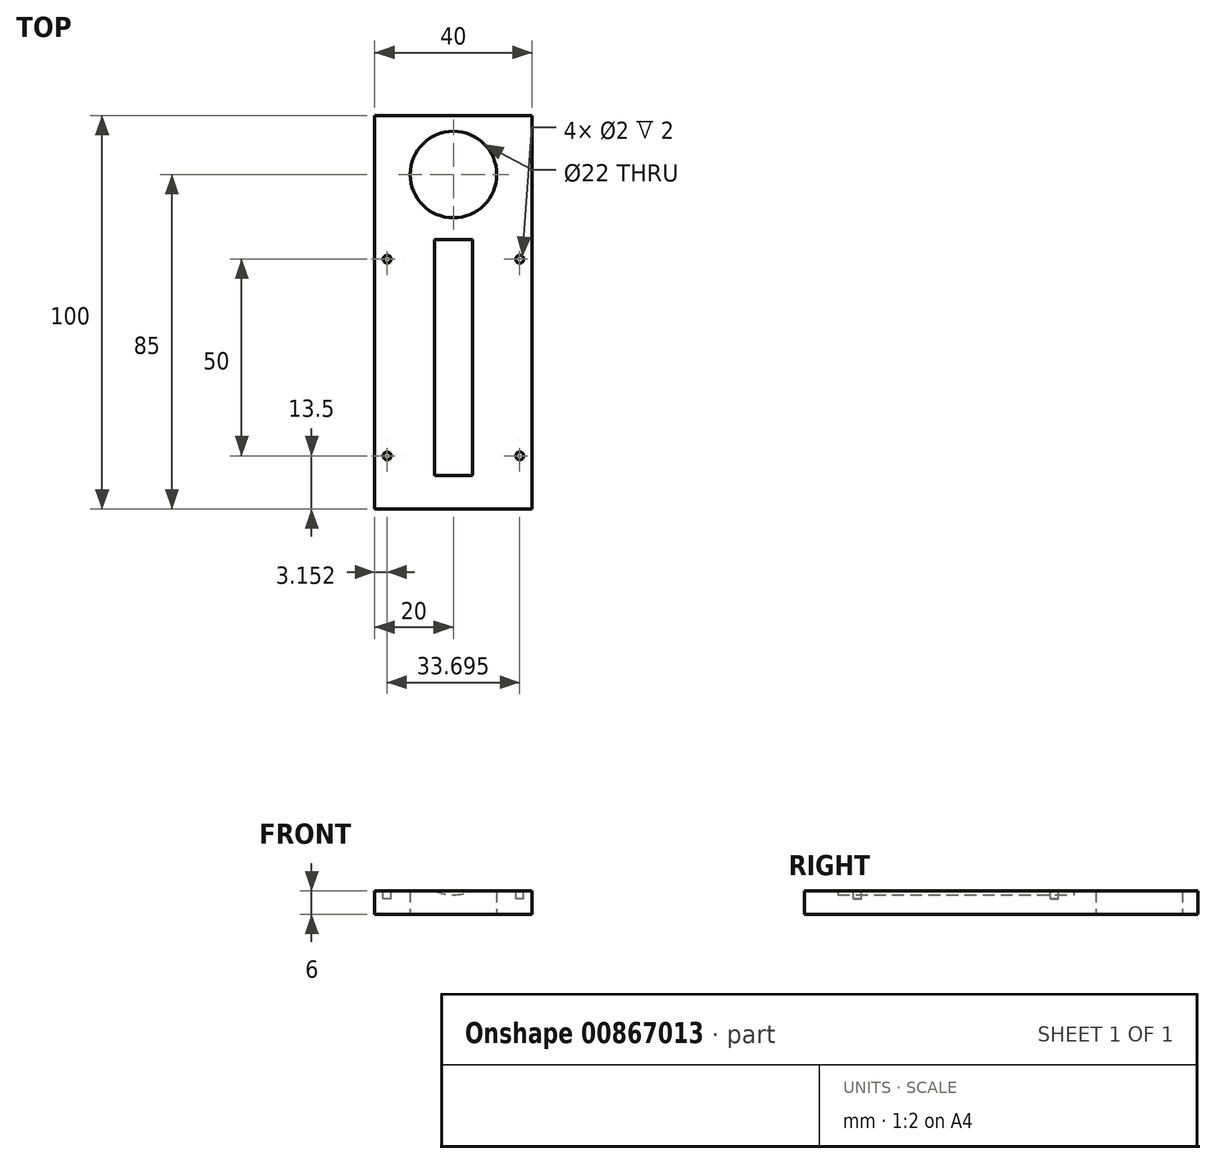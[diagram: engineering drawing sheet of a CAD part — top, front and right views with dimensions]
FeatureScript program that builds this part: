
annotation { "Feature Type Name" : "Feature", "Feature Type Description" : "" }
export const myFeature = defineFeature(function(context is Context, id is Id, definition is map)
    precondition{}
    {
        {
            var Q0;
            Q0=qCreatedBy(makeId("Top.planeOp"),FACE);
            var sketch = newSketch(context, id + "F0", { "sketchPlane" : qUnion([Q0])});
            skLineSegment(sketch, "E0.bottom", {"start": v(20, 15) * mm, "end": v(-20, 15) * mm});
            skLineSegment(sketch, "E0.top", {"start": v(20, -85) * mm, "end": v(-20, -85) * mm});
            skLineSegment(sketch, "E0.left", {"start": v(20, 15) * mm, "end": v(20, -85) * mm});
            skLineSegment(sketch, "E0.right", {"start": v(-20, 15) * mm, "end": v(-20, -85) * mm});
            skPoint(sketch, "E0.middle", {"position": v(0, 0) * mm});
            skCircle(sketch, "E1", {"center": v(0, 0) * mm, "radius": 11 * mm});
            skLineSegment(sketch, "E2", {"start": v(0, 15) * mm, "end": v(0, -33.63) * mm, "construction": true});
            skSolve(sketch);
        }
        {
            var Q0;
            Q0 = qSketchRegion(id + "F0", true);
            extrude(context, id + "F1", {"entities" : qUnion([Q0]), "depth" : 6 * mm, "offsetDistance" : 25 * mm});
        }
        {
            var Q0;
            Q0=qCreatedBy(makeId("Front.planeOp"),FACE);
            var sketch = newSketch(context, id + "F2", { "sketchPlane" : qUnion([Q0])});
            skCircle(sketch, "E3", {"center": v(0, 17.25) * mm, "radius": 12.25 * mm});
            skSolve(sketch);
        }
        {
            var Q0;
            Q0 = qSketchRegion(id + "F2", true);
            extrude(context, id + "F3", {"entities" : qUnion([Q0]), "operationType" : NewBodyOperationType.REMOVE, "depth" : (16.5 + 60) * mm, "offsetDistance" : 25 * mm, "hasSecondDirection" : true, "secondDirectionOppositeDirection" : false, "secondDirectionDepth" : 16.5 * mm});
        }
        {
            var Q0;
            Q0=makeQuery(id+"F1.opExtrude","CAP_FACE",FACE,{"disambiguationData":[OSD([sQuery(id+"F0.wireOp",EDGE,"E0.bottom"),sQuery(id+"F0.wireOp",EDGE,"E0.top"),sQuery(id+"F0.wireOp",EDGE,"E0.left"),sQuery(id+"F0.wireOp",EDGE,"E0.right"),sQuery(id+"F0.wireOp",EDGE,"E1")])],"isStart":false});
            var sketch = newSketch(context, id + "F4", { "sketchPlane" : qUnion([Q0])});
            skCircle(sketch, "E4", {"center": v(-16.85, -21.5) * mm, "radius": 1 * mm});
            skCircle(sketch, "E5", {"center": v(16.85, -21.5) * mm, "radius": 1 * mm});
            skCircle(sketch, "E6", {"center": v(-16.85, -71.5) * mm, "radius": 1 * mm});
            skCircle(sketch, "E7", {"center": v(16.85, -71.5) * mm, "radius": 1 * mm});
            skSolve(sketch);
        }
        {
            var Q0;
            Q0 = qSketchRegion(id + "F4", true);
            extrude(context, id + "F5", {"entities" : qUnion([Q0]), "operationType" : NewBodyOperationType.REMOVE, "oppositeDirection" : true, "depth" : 2 * mm, "offsetDistance" : 25 * mm});
        }
    });
